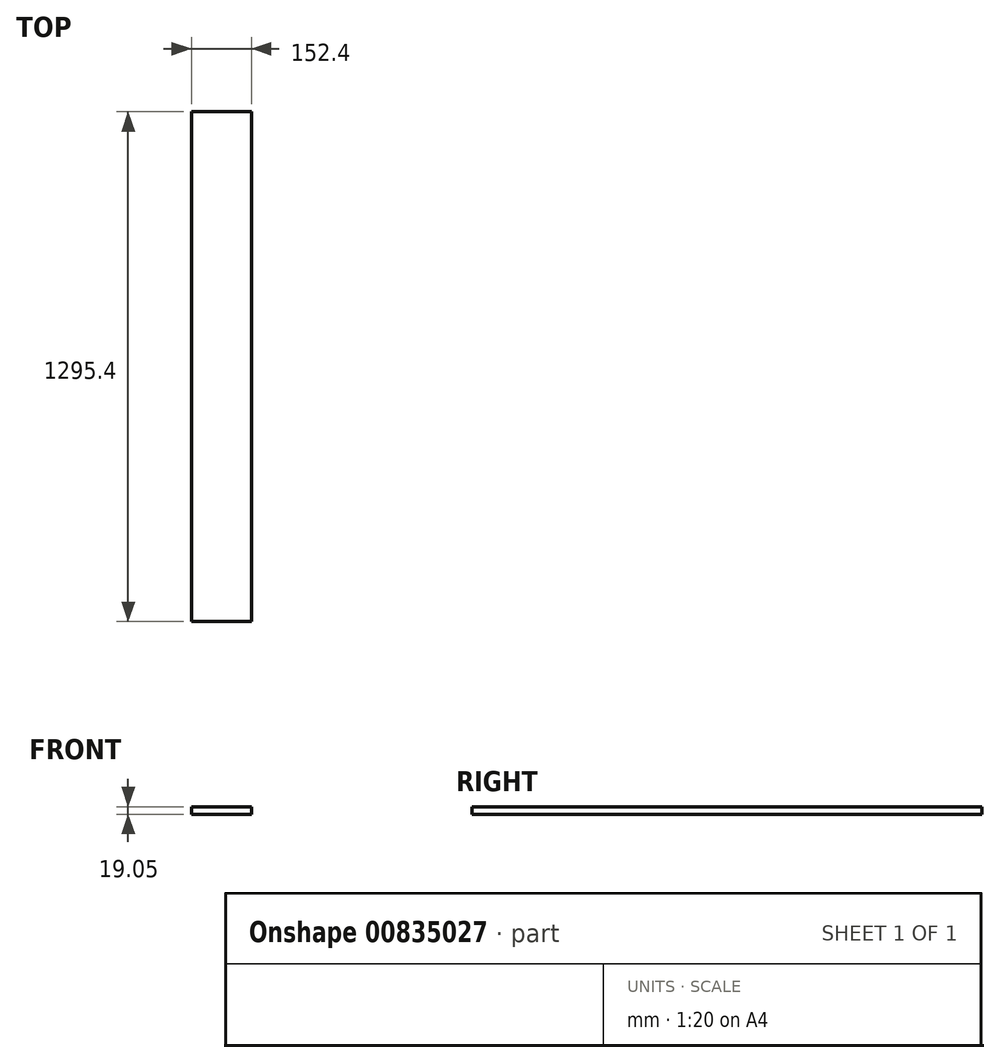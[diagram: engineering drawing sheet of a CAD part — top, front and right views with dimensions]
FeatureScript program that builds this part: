
annotation { "Feature Type Name" : "Feature", "Feature Type Description" : "" }
export const myFeature = defineFeature(function(context is Context, id is Id, definition is map)
    precondition{}
    {
        {
            var Q0;
            Q0=qCreatedBy(makeId("Top.planeOp"),FACE);
            var sketch = newSketch(context, id + "F0", { "sketchPlane" : qUnion([Q0])});
            skLineSegment(sketch, "E0.bottom", {"start": v(0, 0) * mm, "end": v(152.4, 0) * mm});
            skLineSegment(sketch, "E0.top", {"start": v(0, 1295.4) * mm, "end": v(152.4, 1295.4) * mm});
            skLineSegment(sketch, "E0.left", {"start": v(0, 0) * mm, "end": v(0, 1295.4) * mm});
            skLineSegment(sketch, "E0.right", {"start": v(152.4, 0) * mm, "end": v(152.4, 1295.4) * mm});
            skSolve(sketch);
        }
        {
            var Q0;
            Q0 = qSketchRegion(id + "F0", true);
            extrude(context, id + "F1", {"entities" : qUnion([Q0]), "depth" : 19.05 * mm, "offsetDistance" : 25.4 * mm});
        }
    });
